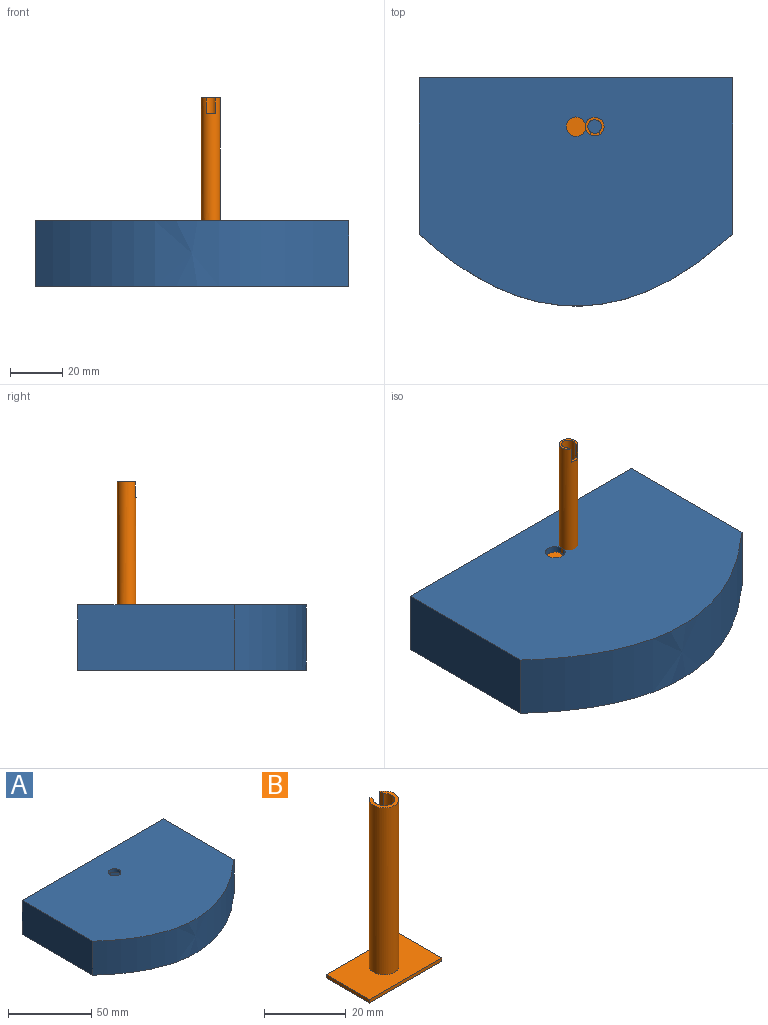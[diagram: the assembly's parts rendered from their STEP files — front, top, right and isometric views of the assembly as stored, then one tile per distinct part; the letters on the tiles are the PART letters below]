
ASSEMBLY  parts=2 mates=1
PART A: 16 faces, bbox 120x97.8x25 mm
  f0: plane 60x25mm, normal (1,0,0), area 1371.2mm2, adj f2,f4,f5,f6,f12,f13,f14,f15
  f1: plane 56.4x22.5mm, normal (-1,0,0), area 1140.1mm2, adj f2,f8,f9,f10,f12,f13,f14,f15
  f2: plane 120x97.81mm, normal (0,0,-1), area 915.2mm2, adj f0,f1,f3,f4,f5,f7,f8,f9
  f3: plane 60x25mm, normal (-1,0,0), area 1500mm2, adj f2,f4,f5,f6
  f4: extruded ~120x27.5mm, area 3378.6mm2, adj f0,f2,f3,f6
  f5: plane 120x25mm, normal (0,1,0), area 3000mm2, adj f0,f2,f3,f6
  f6: plane 120x97.81mm, normal (0,0,1), area 9355.8mm2, adj f0,f3,f4,f5,f11
  f7: plane 56.4x22.5mm, normal (1,0,0), area 1268.9mm2, adj f2,f8,f9,f10
  f8: extruded ~115x26.11mm, area 2908mm2, adj f1,f2,f7,f10
  f9: plane 115x22.5mm, normal (0,-1,0), area 2587.5mm2, adj f1,f2,f7,f10
  f10: plane 115x82.54mm, normal (0,0,-1), area 8440.6mm2, adj f1,f7,f8,f9,f11
  f11: cylinder r=3.75mm len=7.5mm, axis (0,0,1), area 58.9mm2, adj f6,f10
  f12: plane 9.2x2.5mm, normal (0,-1,0), area 23mm2, adj f0,f1,f13,f15
  f13: plane 14x2.5mm, normal (0,0,-1), area 35mm2, adj f0,f1,f12,f14
  f14: plane 9.2x2.5mm, normal (0,1,0), area 23mm2, adj f0,f1,f13,f15
  f15: plane 14x2.5mm, normal (0,0,1), area 35mm2, adj f0,f1,f12,f14
PART B: 12 faces, bbox 25x15x51 mm
  f0: cylinder r=3.6mm len=50mm, axis (0,0,-1), area 1109.2mm2, adj f1,f7,f9,f10,f11
  f1: plane 7.2x6.75mm, normal (0,0,1), area 15.8mm2, adj f0,f2,f9,f10
  f2: cylinder r=2.6mm len=51mm, axis (0,0,1), area 810.2mm2, adj f1,f8,f9,f10,f11
  f3: plane 25x1mm, normal (0,-1,0), area 25mm2, adj f4,f6,f7,f8
  f4: plane 15x1mm, normal (1,0,0), area 15mm2, adj f3,f5,f7,f8
  f5: plane 25x1mm, normal (0,1,0), area 25mm2, adj f4,f6,f7,f8
  f6: plane 15x1mm, normal (-1,0,0), area 15mm2, adj f3,f5,f7,f8
  f7: plane 25x15mm, normal (0,0,1), area 334.3mm2, adj f0,f3,f4,f5,f6
  f8: plane 25x15mm, normal (0,0,-1), area 353.8mm2, adj f2,f3,f4,f5,f6
  f9: plane 6x1.22mm, normal (1,0,0), area 7.3mm2, adj f0,f1,f2,f11
  f10: plane 6x1.22mm, normal (-1,0,0), area 7.3mm2, adj f0,f1,f2,f11
  f11: plane 3.48x1.67mm, normal (0,0,1), area 3.7mm2, adj f0,f2,f9,f10
PLACE A t=(0.26,108.19,-102.2)mm
PLACE B rot(axis=(0,0,-1),180deg) t=(7.43,119.44,-81)mm
MATE pin_slot A.f11 <-> B.f0  axis (0,0,1) through (0.26,119.44,-77.2)mm
